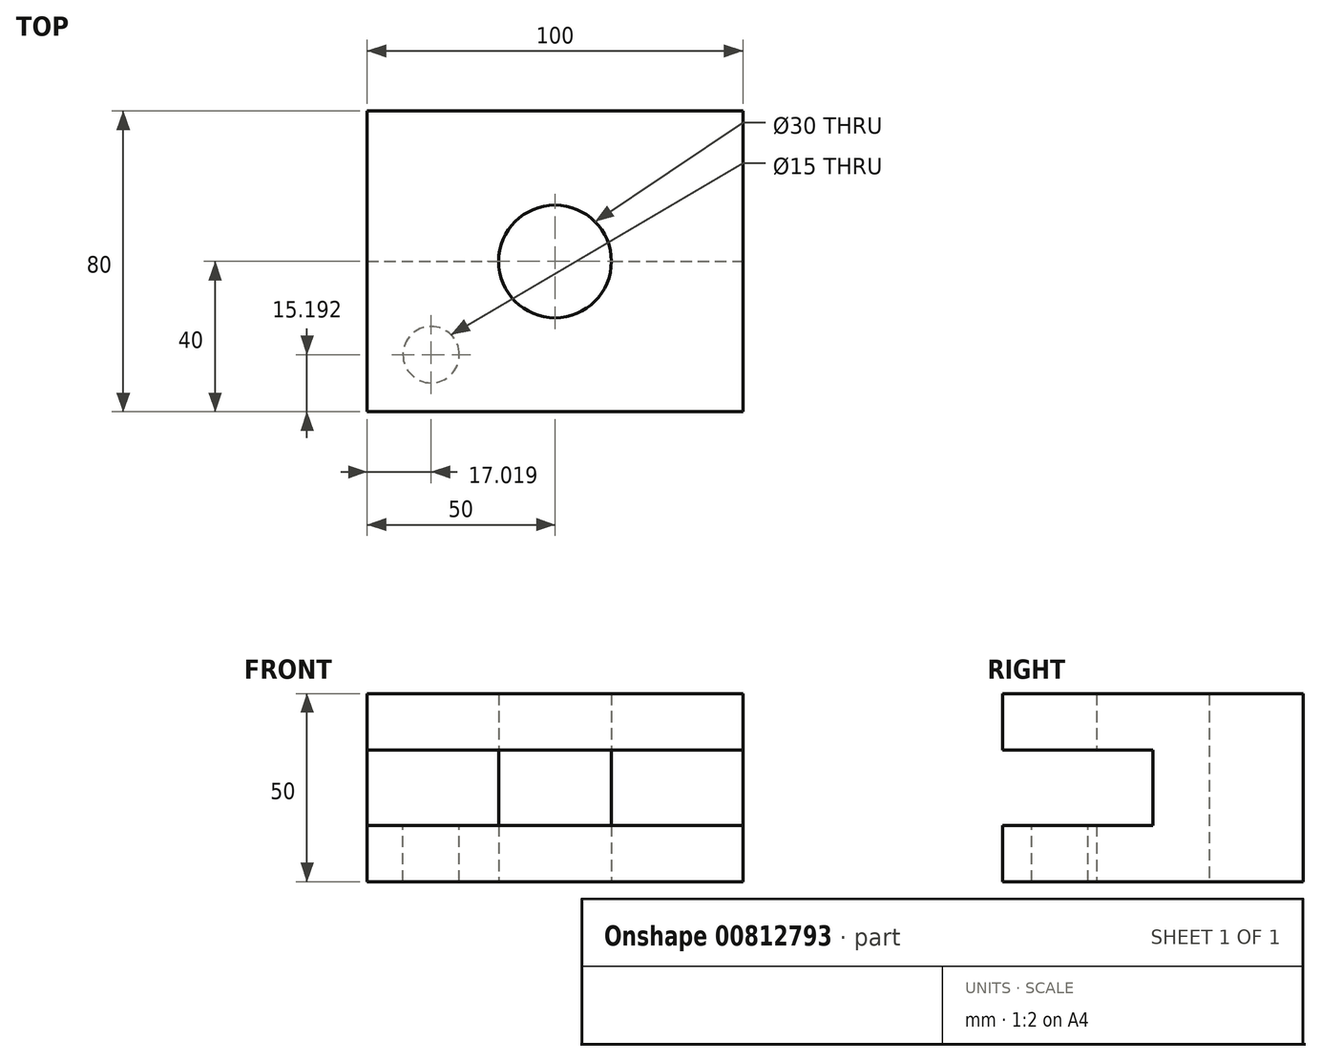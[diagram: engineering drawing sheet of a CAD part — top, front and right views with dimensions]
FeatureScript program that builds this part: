
annotation { "Feature Type Name" : "Feature", "Feature Type Description" : "" }
export const myFeature = defineFeature(function(context is Context, id is Id, definition is map)
    precondition{}
    {
        {
            var Q0;
            Q0=qCreatedBy(makeId("Top.planeOp"),FACE);
            var sketch = newSketch(context, id + "F0", { "sketchPlane" : qUnion([Q0])});
            skLineSegment(sketch, "E0.bottom", {"start": v(-50, -40) * mm, "end": v(50, -40) * mm});
            skLineSegment(sketch, "E0.top", {"start": v(-50, 40) * mm, "end": v(50, 40) * mm});
            skLineSegment(sketch, "E0.left", {"start": v(-50, -40) * mm, "end": v(-50, 40) * mm});
            skLineSegment(sketch, "E0.right", {"start": v(50, -40) * mm, "end": v(50, 40) * mm});
            skCircle(sketch, "E1", {"center": v(0, 0) * mm, "radius": 15 * mm});
            skSolve(sketch);
        }
        {
            var Q0;
            Q0=makeQuery(id+"F0.imprint","IMPRINT",FACE,{"disambiguationData":[TD([[makeQuery(id+"F0.imprint","IMPRINT",EDGE,{"derivedFrom":sQuery(id+"F0.wireOp",EDGE,"E0.bottom")}),1.0]])]});
            extrude(context, id + "F1", {"entities" : qUnion([Q0]), "depth" : 50 * mm, "offsetDistance" : 25 * mm});
        }
        {
            var Q0;
            Q0=makeQuery(id+"F1.opExtrude","SWEPT_FACE",FACE,{"disambiguationData":[OSD([sQuery(id+"F0.wireOp",EDGE,"E0.bottom")])]});
            var sketch = newSketch(context, id + "F2", { "sketchPlane" : qUnion([Q0])});
            skLineSegment(sketch, "E2.bottom", {"start": v(-56.06, 35) * mm, "end": v(63.94, 35) * mm});
            skLineSegment(sketch, "E2.top", {"start": v(-56.06, 15) * mm, "end": v(63.94, 15) * mm});
            skLineSegment(sketch, "E2.left", {"start": v(-56.06, 35) * mm, "end": v(-56.06, 15) * mm});
            skLineSegment(sketch, "E2.right", {"start": v(63.94, 35) * mm, "end": v(63.94, 15) * mm});
            skSolve(sketch);
        }
        {
            var Q0;
            Q0 = qSketchRegion(id + "F2", true);
            extrude(context, id + "F3", {"entities" : qUnion([Q0]), "operationType" : NewBodyOperationType.REMOVE, "oppositeDirection" : true, "depth" : 40 * mm, "offsetDistance" : 25 * mm});
        }
        {
            var Q0;
            Q0=makeQuery(id+"F3.boolean.opBoolean","COPY",FACE,{"derivedFrom":makeQuery(id+"F3.opExtrude","SWEPT_FACE",FACE,{"disambiguationData":[OSD([sQuery(id+"F2.wireOp",EDGE,"E2.top")])]})});
            var sketch = newSketch(context, id + "F4", { "sketchPlane" : qUnion([Q0])});
            skCircle(sketch, "E3", {"center": v(-32.98, -24.8) * mm, "radius": 7.5 * mm});
            skCircle(sketch, "E4.MirrorC", {"center": v(32.98, -24.8) * mm, "radius": 7.5 * mm});
            skSolve(sketch);
        }
        {
            var Q0;
            Q0=makeQuery(id+"F4.imprint","IMPRINT",FACE,{"disambiguationData":[TD([[makeQuery(id+"F4.imprint","IMPRINT",EDGE,{"derivedFrom":sQuery(id+"F4.wireOp",EDGE,"E3")}),1.0]])]});
            extrude(context, id + "F5", {"entities" : qUnion([Q0]), "operationType" : NewBodyOperationType.REMOVE, "oppositeDirection" : true, "depth" : 25 * mm, "offsetDistance" : 25 * mm});
        }
    });
